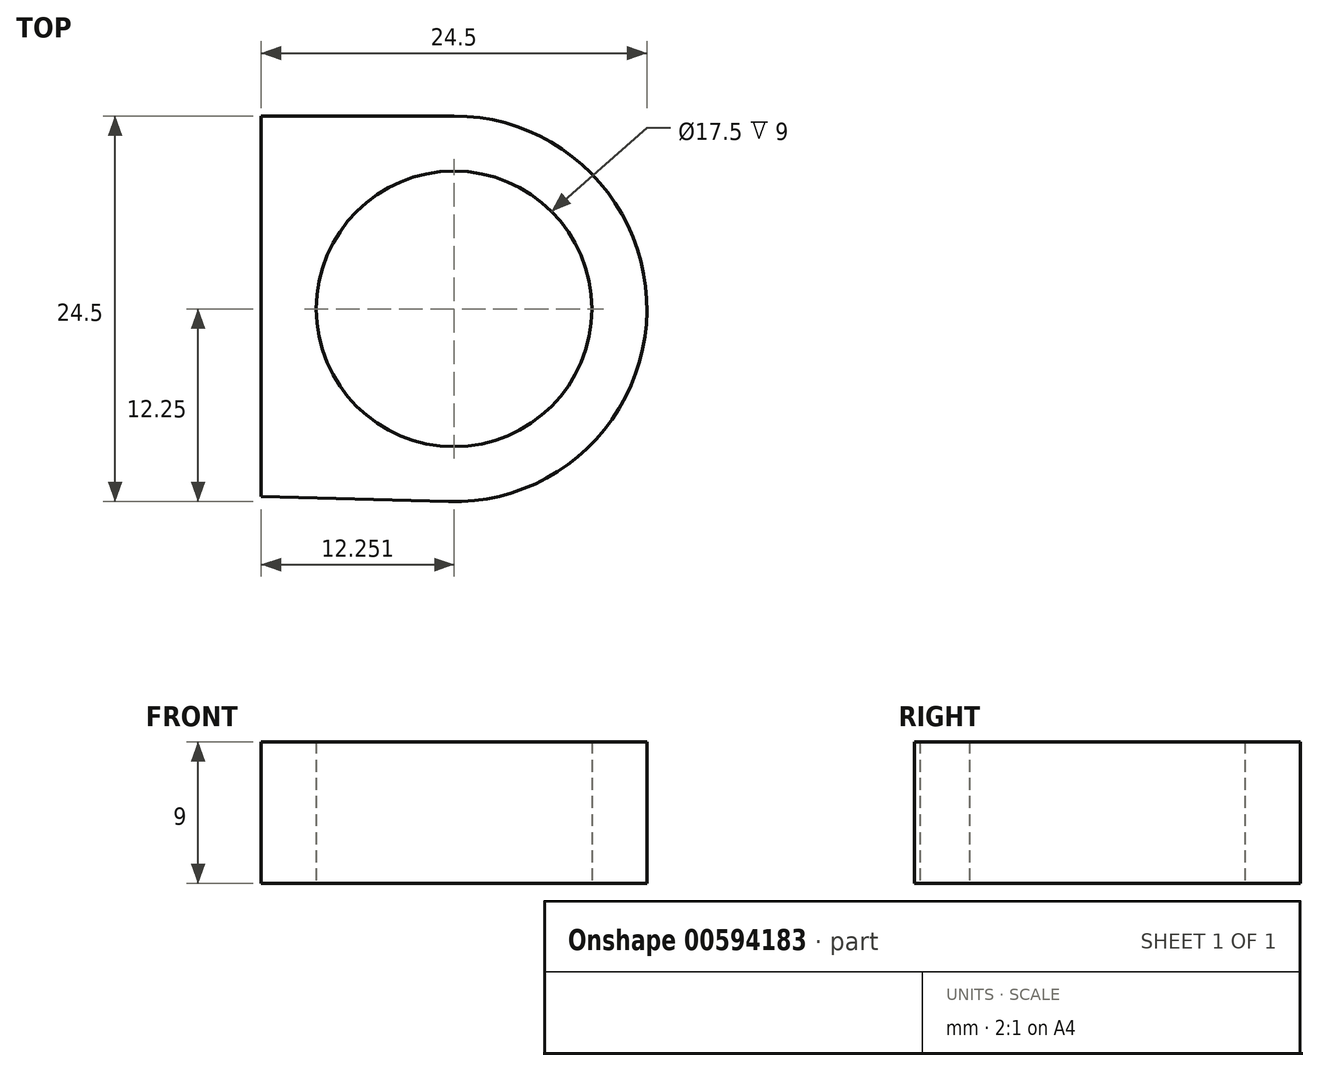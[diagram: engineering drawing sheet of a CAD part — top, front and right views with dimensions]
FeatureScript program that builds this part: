
annotation { "Feature Type Name" : "Feature", "Feature Type Description" : "" }
export const myFeature = defineFeature(function(context is Context, id is Id, definition is map)
    precondition{}
    {
        {
            var Q0;
            Q0=qCreatedBy(makeId("Top.planeOp"),FACE);
            var sketch = newSketch(context, id + "F0", { "sketchPlane" : qUnion([Q0])});
            skCircle(sketch, "E0", {"center": v(-43.37, 33.1) * mm, "radius": 8.75 * mm});
            skCircle(sketch, "E1", {"center": v(-43.37, 33.1) * mm, "radius": 12.25 * mm});
            skLineSegment(sketch, "E2", {"start": v(-55.62, 21.2) * mm, "end": v(-43.37, 20.85) * mm});
            skLineSegment(sketch, "E3", {"start": v(-43.37, 45.36) * mm, "end": v(-55.62, 45.36) * mm});
            skLineSegment(sketch, "E4", {"start": v(-55.62, 45.36) * mm, "end": v(-55.62, 21.2) * mm});
            skSolve(sketch);
        }
        {
            var Q0;
            {var subQ0=sQuery(id+"F0.wireOp",EDGE,"E3");Q0=makeQuery(id+"F0.imprint","IMPRINT",FACE,{"disambiguationData":[TD([[makeQuery(id+"F0.imprint","IMPRINT",EDGE,{"derivedFrom":subQ0}),1.0]])]});}
            var Q1;
            {var subQ0=sQuery(id+"F0.wireOp",EDGE,"E2");var subQ1=sQuery(id+"F0.wireOp",EDGE,"E1");var subQ2=makeQuery(id+"F0.imprint","INTERSECT",VERTEX,{"derivedFrom":[subQ1,subQ0]});Q1=makeQuery(id+"F0.imprint","IMPRINT",FACE,{"disambiguationData":[TD([[makeQuery(id+"F0.imprint","IMPRINT",EDGE,{"disambiguationData":[TD([[subQ2,1.0]])],"derivedFrom":subQ1}),-1.0]])]});}
            var Q2;
            Q2=makeQuery(id+"F0.imprint","IMPRINT",FACE,{"disambiguationData":[TD([[makeQuery(id+"F0.imprint","IMPRINT",EDGE,{"derivedFrom":sQuery(id+"F0.wireOp",EDGE,"E0")}),-1.0]])]});
            extrude(context, id + "F1", {"entities" : qUnion([Q0, Q1, Q2]), "depth" : 9 * mm, "offsetDistance" : 25 * mm});
        }
    });
